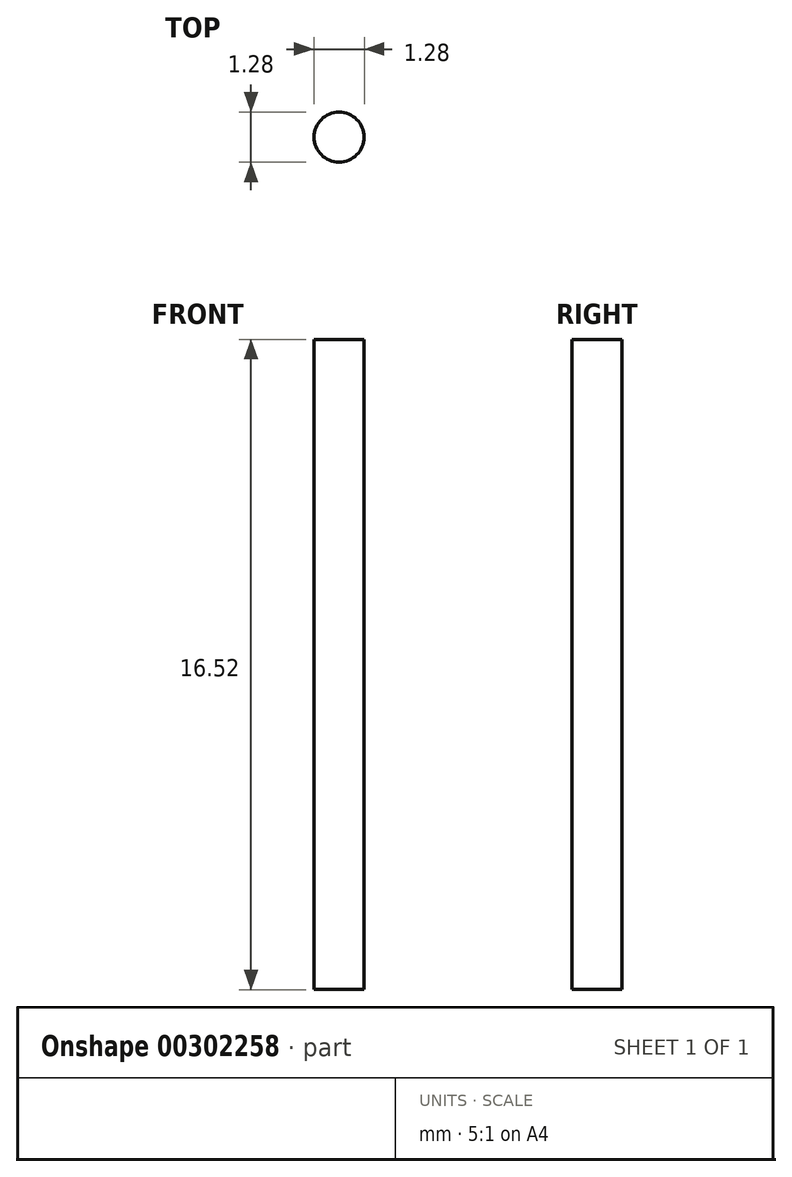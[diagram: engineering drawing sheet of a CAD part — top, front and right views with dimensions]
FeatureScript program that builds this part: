
annotation { "Feature Type Name" : "Feature", "Feature Type Description" : "" }
export const myFeature = defineFeature(function(context is Context, id is Id, definition is map)
    precondition{}
    {
        {
            var Q0;
            Q0=qCreatedBy(makeId("Top.planeOp"),FACE);
            var sketch = newSketch(context, id + "F0", { "sketchPlane" : qUnion([Q0])});
            skCircle(sketch, "E0", {"center": v(0, 0) * mm, "radius": 0.64 * mm});
            skSolve(sketch);
        }
        {
            var Q0;
            Q0 = qSketchRegion(id + "F0", true);
            extrude(context, id + "F1", {"entities" : qUnion([Q0]), "endBound" : BoundingType.SYMMETRIC, "depth" : 16.5 * mm});
        }
    });
